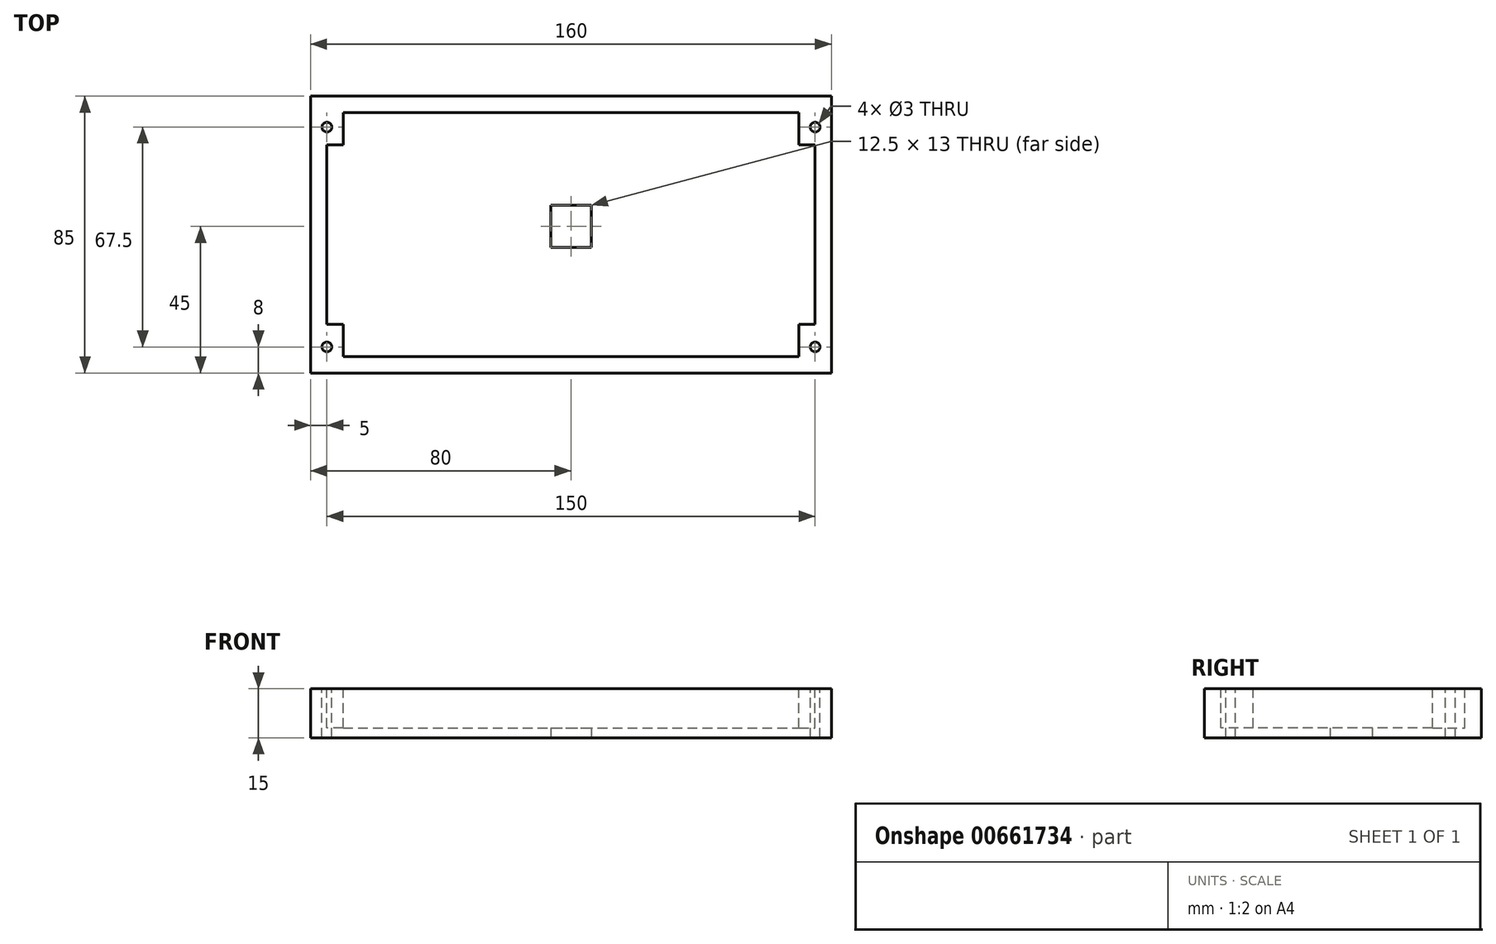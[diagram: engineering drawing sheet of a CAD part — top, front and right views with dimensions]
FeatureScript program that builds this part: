
annotation { "Feature Type Name" : "Feature", "Feature Type Description" : "" }
export const myFeature = defineFeature(function(context is Context, id is Id, definition is map)
    precondition{}
    {
        {
            var Q0;
            Q0=qCreatedBy(makeId("Top.planeOp"),FACE);
            var sketch = newSketch(context, id + "F0", { "sketchPlane" : qUnion([Q0])});
            skLineSegment(sketch, "E0.bottom", {"start": v(-6.25, 6.5) * mm, "end": v(6.25, 6.5) * mm});
            skLineSegment(sketch, "E0.top", {"start": v(-6.25, -6.5) * mm, "end": v(6.25, -6.5) * mm});
            skLineSegment(sketch, "E0.left", {"start": v(-6.25, 6.5) * mm, "end": v(-6.25, -6.5) * mm});
            skLineSegment(sketch, "E0.right", {"start": v(6.25, 6.5) * mm, "end": v(6.25, -6.5) * mm});
            skLineSegment(sketch, "E1.bottom", {"start": v(-80, 40) * mm, "end": v(80, 40) * mm});
            skLineSegment(sketch, "E1.top", {"start": v(-80, -45) * mm, "end": v(80, -45) * mm});
            skLineSegment(sketch, "E1.left", {"start": v(-80, 40) * mm, "end": v(-80, -45) * mm});
            skLineSegment(sketch, "E1.right", {"start": v(80, 40) * mm, "end": v(80, -45) * mm});
            skSolve(sketch);
        }
        {
            var Q0;
            Q0=makeQuery(id+"F0.imprint","IMPRINT",FACE,{"disambiguationData":[TD([[makeQuery(id+"F0.imprint","IMPRINT",EDGE,{"derivedFrom":sQuery(id+"F0.wireOp",EDGE,"E0.bottom")}),1.0]])]});
            extrude(context, id + "F1", {"entities" : qUnion([Q0]), "depth" : 3 * mm, "offsetDistance" : 25 * mm});
        }
        {
            var Q0;
            Q0=makeQuery(id+"F1.opExtrude","CAP_FACE",FACE,{"disambiguationData":[OSD([sQuery(id+"F0.wireOp",EDGE,"E0.bottom"),sQuery(id+"F0.wireOp",EDGE,"E0.top"),sQuery(id+"F0.wireOp",EDGE,"E0.left"),sQuery(id+"F0.wireOp",EDGE,"E0.right"),sQuery(id+"F0.wireOp",EDGE,"E1.bottom"),sQuery(id+"F0.wireOp",EDGE,"E1.top"),sQuery(id+"F0.wireOp",EDGE,"E1.left"),sQuery(id+"F0.wireOp",EDGE,"E1.right")])],"isStart":false});
            var sketch = newSketch(context, id + "F2", { "sketchPlane" : qUnion([Q0])});
            skLineSegment(sketch, "E2.bottom", {"start": v(-75, 35) * mm, "end": v(75, 35) * mm});
            skLineSegment(sketch, "E2.top", {"start": v(-75, -40) * mm, "end": v(75, -40) * mm});
            skLineSegment(sketch, "E2.left", {"start": v(-75, 35) * mm, "end": v(-75, -40) * mm});
            skLineSegment(sketch, "E2.right", {"start": v(75, 35) * mm, "end": v(75, -40) * mm});
            skSolve(sketch);
        }
        {
            var Q0;
            Q0=makeQuery(id+"F2.imprint","IMPRINT",FACE,{"disambiguationData":[TD([[makeQuery(id+"F2.imprint","IMPRINT",EDGE,{"derivedFrom":sQuery(id+"F2.wireOp",EDGE,"E2.bottom")}),1.0]])]});
            extrude(context, id + "F3", {"entities" : qUnion([Q0]), "operationType" : NewBodyOperationType.ADD, "depth" : 12 * mm, "offsetDistance" : 25 * mm});
        }
        {
            var Q0;
            Q0=makeQuery(id+"F3.opExtrude","CAP_FACE",FACE,{"disambiguationData":[OSD([sQuery(id+"F0.wireOp",EDGE,"E1.bottom"),sQuery(id+"F0.wireOp",EDGE,"E1.top"),sQuery(id+"F0.wireOp",EDGE,"E1.left"),sQuery(id+"F0.wireOp",EDGE,"E1.right"),sQuery(id+"F2.wireOp",EDGE,"E2.bottom"),sQuery(id+"F2.wireOp",EDGE,"E2.top"),sQuery(id+"F2.wireOp",EDGE,"E2.left"),sQuery(id+"F2.wireOp",EDGE,"E2.right")])],"isStart":false});
            var sketch = newSketch(context, id + "F4", { "sketchPlane" : qUnion([Q0])});
            skCircle(sketch, "E3", {"center": v(-75, 30.5) * mm, "radius": 1.5 * mm});
            skCircle(sketch, "E4", {"center": v(75, 30.5) * mm, "radius": 1.5 * mm});
            skCircle(sketch, "E5", {"center": v(75, -37) * mm, "radius": 1.5 * mm});
            skCircle(sketch, "E6", {"center": v(-75, -37) * mm, "radius": 1.5 * mm});
            skLineSegment(sketch, "E7.bottom", {"start": v(-75, 35) * mm, "end": v(-70, 35) * mm});
            skLineSegment(sketch, "E7.top", {"start": v(-75, 25) * mm, "end": v(-70, 25) * mm});
            skLineSegment(sketch, "E7.left", {"start": v(-75, 35) * mm, "end": v(-75, 25) * mm});
            skLineSegment(sketch, "E7.right", {"start": v(-70, 35) * mm, "end": v(-70, 25) * mm});
            skLineSegment(sketch, "E8.bottom", {"start": v(75, -40) * mm, "end": v(70, -40) * mm});
            skLineSegment(sketch, "E8.top", {"start": v(75, -30) * mm, "end": v(70, -30) * mm});
            skLineSegment(sketch, "E8.left", {"start": v(75, -40) * mm, "end": v(75, -30) * mm});
            skLineSegment(sketch, "E8.right", {"start": v(70, -40) * mm, "end": v(70, -30) * mm});
            skLineSegment(sketch, "E9.bottom", {"start": v(-75, -40) * mm, "end": v(-70, -40) * mm});
            skLineSegment(sketch, "E9.top", {"start": v(-75, -30) * mm, "end": v(-70, -30) * mm});
            skLineSegment(sketch, "E9.left", {"start": v(-75, -40) * mm, "end": v(-75, -30) * mm});
            skLineSegment(sketch, "E9.right", {"start": v(-70, -40) * mm, "end": v(-70, -30) * mm});
            skLineSegment(sketch, "E10.bottom", {"start": v(75, 35) * mm, "end": v(70, 35) * mm});
            skLineSegment(sketch, "E10.top", {"start": v(75, 25) * mm, "end": v(70, 25) * mm});
            skLineSegment(sketch, "E10.left", {"start": v(75, 35) * mm, "end": v(75, 25) * mm});
            skLineSegment(sketch, "E10.right", {"start": v(70, 35) * mm, "end": v(70, 25) * mm});
            skSolve(sketch);
        }
        {
            var Q0;
            {var subQ1=sQuery(id+"F4.wireOp",EDGE,"E10.bottom");Q0=makeQuery(id+"F4.imprint","IMPRINT",FACE,{"disambiguationData":[TD([[makeQuery(id+"F4.imprint","IMPRINT",EDGE,{"derivedFrom":subQ1}),-1.0]])]});}
            var Q1;
            {var subQ1=sQuery(id+"F4.wireOp",EDGE,"E7.bottom");Q1=makeQuery(id+"F4.imprint","IMPRINT",FACE,{"disambiguationData":[TD([[makeQuery(id+"F4.imprint","IMPRINT",EDGE,{"derivedFrom":subQ1}),-1.0]])]});}
            var Q2;
            {var subQ1=sQuery(id+"F4.wireOp",EDGE,"E9.bottom");Q2=makeQuery(id+"F4.imprint","IMPRINT",FACE,{"disambiguationData":[TD([[makeQuery(id+"F4.imprint","IMPRINT",EDGE,{"derivedFrom":subQ1}),1.0]])]});}
            var Q3;
            {var subQ5=sQuery(id+"F4.wireOp",EDGE,"E8.bottom");Q3=makeQuery(id+"F4.imprint","IMPRINT",FACE,{"disambiguationData":[TD([[makeQuery(id+"F4.imprint","IMPRINT",EDGE,{"derivedFrom":subQ5}),1.0]])]});}
            var Q4;
            Q4=makeQuery(id+"F1.opExtrude","CAP_FACE",FACE,{"disambiguationData":[OSD([sQuery(id+"F0.wireOp",EDGE,"E0.bottom"),sQuery(id+"F0.wireOp",EDGE,"E0.top"),sQuery(id+"F0.wireOp",EDGE,"E0.left"),sQuery(id+"F0.wireOp",EDGE,"E0.right"),sQuery(id+"F0.wireOp",EDGE,"E1.bottom"),sQuery(id+"F0.wireOp",EDGE,"E1.top"),sQuery(id+"F0.wireOp",EDGE,"E1.left"),sQuery(id+"F0.wireOp",EDGE,"E1.right")])],"isStart":false});
            extrude(context, id + "F5", {"entities" : qUnion([Q0, Q1, Q2, Q3]), "operationType" : NewBodyOperationType.ADD, "endBound" : BoundingType.UP_TO_SURFACE, "oppositeDirection" : true, "depth" : 25 * mm, "endBoundEntityFace" : qUnion([Q4]), "offsetDistance" : 25 * mm});
        }
        {
            var Q0;
            {var subQ0=sQuery(id+"F4.wireOp",EDGE,"E9.left");var subQ1=sQuery(id+"F4.wireOp",EDGE,"E6");var subQ2=makeQuery(id+"F4.imprint","INTERSECT",VERTEX,{"disambiguationData":[OD(0.0)],"derivedFrom":[subQ1,subQ0]});Q0=makeQuery(id+"F4.imprint","IMPRINT",FACE,{"disambiguationData":[TD([[makeQuery(id+"F4.imprint","IMPRINT",EDGE,{"disambiguationData":[TD([[subQ2,-1.0]])],"derivedFrom":subQ1}),1.0]])]});}
            var Q1;
            {var subQ0=sQuery(id+"F4.wireOp",EDGE,"E9.left");var subQ1=sQuery(id+"F4.wireOp",EDGE,"E6");var subQ2=makeQuery(id+"F4.imprint","INTERSECT",VERTEX,{"disambiguationData":[OD(0.0)],"derivedFrom":[subQ1,subQ0]});Q1=makeQuery(id+"F4.imprint","IMPRINT",FACE,{"disambiguationData":[TD([[makeQuery(id+"F4.imprint","IMPRINT",EDGE,{"disambiguationData":[TD([[subQ2,1.0]])],"derivedFrom":subQ1}),1.0]])]});}
            var Q2;
            {var subQ0=sQuery(id+"F4.wireOp",EDGE,"E8.left");var subQ1=sQuery(id+"F4.wireOp",EDGE,"E5");var subQ2=makeQuery(id+"F4.imprint","INTERSECT",VERTEX,{"disambiguationData":[OD(0.0)],"derivedFrom":[subQ1,subQ0]});Q2=makeQuery(id+"F4.imprint","IMPRINT",FACE,{"disambiguationData":[TD([[makeQuery(id+"F4.imprint","IMPRINT",EDGE,{"disambiguationData":[TD([[subQ2,-1.0]])],"derivedFrom":subQ1}),1.0]])]});}
            var Q3;
            {var subQ0=sQuery(id+"F4.wireOp",EDGE,"E8.left");var subQ1=sQuery(id+"F4.wireOp",EDGE,"E5");var subQ2=makeQuery(id+"F4.imprint","INTERSECT",VERTEX,{"disambiguationData":[OD(0.0)],"derivedFrom":[subQ1,subQ0]});Q3=makeQuery(id+"F4.imprint","IMPRINT",FACE,{"disambiguationData":[TD([[makeQuery(id+"F4.imprint","IMPRINT",EDGE,{"disambiguationData":[TD([[subQ2,1.0]])],"derivedFrom":subQ1}),1.0]])]});}
            var Q4;
            {var subQ0=sQuery(id+"F4.wireOp",EDGE,"E10.left");var subQ1=sQuery(id+"F4.wireOp",EDGE,"E4");var subQ2=makeQuery(id+"F4.imprint","INTERSECT",VERTEX,{"disambiguationData":[OD(0.0)],"derivedFrom":[subQ1,subQ0]});Q4=makeQuery(id+"F4.imprint","IMPRINT",FACE,{"disambiguationData":[TD([[makeQuery(id+"F4.imprint","IMPRINT",EDGE,{"disambiguationData":[TD([[subQ2,1.0]])],"derivedFrom":subQ1}),1.0]])]});}
            var Q5;
            {var subQ0=sQuery(id+"F4.wireOp",EDGE,"E10.left");var subQ1=sQuery(id+"F4.wireOp",EDGE,"E4");var subQ2=makeQuery(id+"F4.imprint","INTERSECT",VERTEX,{"disambiguationData":[OD(0.0)],"derivedFrom":[subQ1,subQ0]});Q5=makeQuery(id+"F4.imprint","IMPRINT",FACE,{"disambiguationData":[TD([[makeQuery(id+"F4.imprint","IMPRINT",EDGE,{"disambiguationData":[TD([[subQ2,-1.0]])],"derivedFrom":subQ1}),1.0]])]});}
            var Q6;
            {var subQ0=sQuery(id+"F4.wireOp",EDGE,"E7.left");var subQ1=sQuery(id+"F4.wireOp",EDGE,"E3");var subQ2=makeQuery(id+"F4.imprint","INTERSECT",VERTEX,{"disambiguationData":[OD(0.0)],"derivedFrom":[subQ1,subQ0]});Q6=makeQuery(id+"F4.imprint","IMPRINT",FACE,{"disambiguationData":[TD([[makeQuery(id+"F4.imprint","IMPRINT",EDGE,{"disambiguationData":[TD([[subQ2,-1.0]])],"derivedFrom":subQ1}),1.0]])]});}
            var Q7;
            {var subQ0=sQuery(id+"F4.wireOp",EDGE,"E7.left");var subQ1=sQuery(id+"F4.wireOp",EDGE,"E3");var subQ2=makeQuery(id+"F4.imprint","INTERSECT",VERTEX,{"disambiguationData":[OD(0.0)],"derivedFrom":[subQ1,subQ0]});Q7=makeQuery(id+"F4.imprint","IMPRINT",FACE,{"disambiguationData":[TD([[makeQuery(id+"F4.imprint","IMPRINT",EDGE,{"disambiguationData":[TD([[subQ2,1.0]])],"derivedFrom":subQ1}),1.0]])]});}
            var Q8;
            Q8=makeQuery(id+"F1.opExtrude","CAP_FACE",FACE,{"disambiguationData":[OSD([sQuery(id+"F0.wireOp",EDGE,"E0.bottom"),sQuery(id+"F0.wireOp",EDGE,"E0.top"),sQuery(id+"F0.wireOp",EDGE,"E0.left"),sQuery(id+"F0.wireOp",EDGE,"E0.right"),sQuery(id+"F0.wireOp",EDGE,"E1.bottom"),sQuery(id+"F0.wireOp",EDGE,"E1.top"),sQuery(id+"F0.wireOp",EDGE,"E1.left"),sQuery(id+"F0.wireOp",EDGE,"E1.right")])],"isStart":true});
            extrude(context, id + "F6", {"entities" : qUnion([Q0, Q1, Q2, Q3, Q4, Q5, Q6, Q7]), "operationType" : NewBodyOperationType.REMOVE, "endBound" : BoundingType.UP_TO_SURFACE, "oppositeDirection" : true, "depth" : 25 * mm, "endBoundEntityFace" : qUnion([Q8]), "offsetDistance" : 25 * mm});
        }
    });
